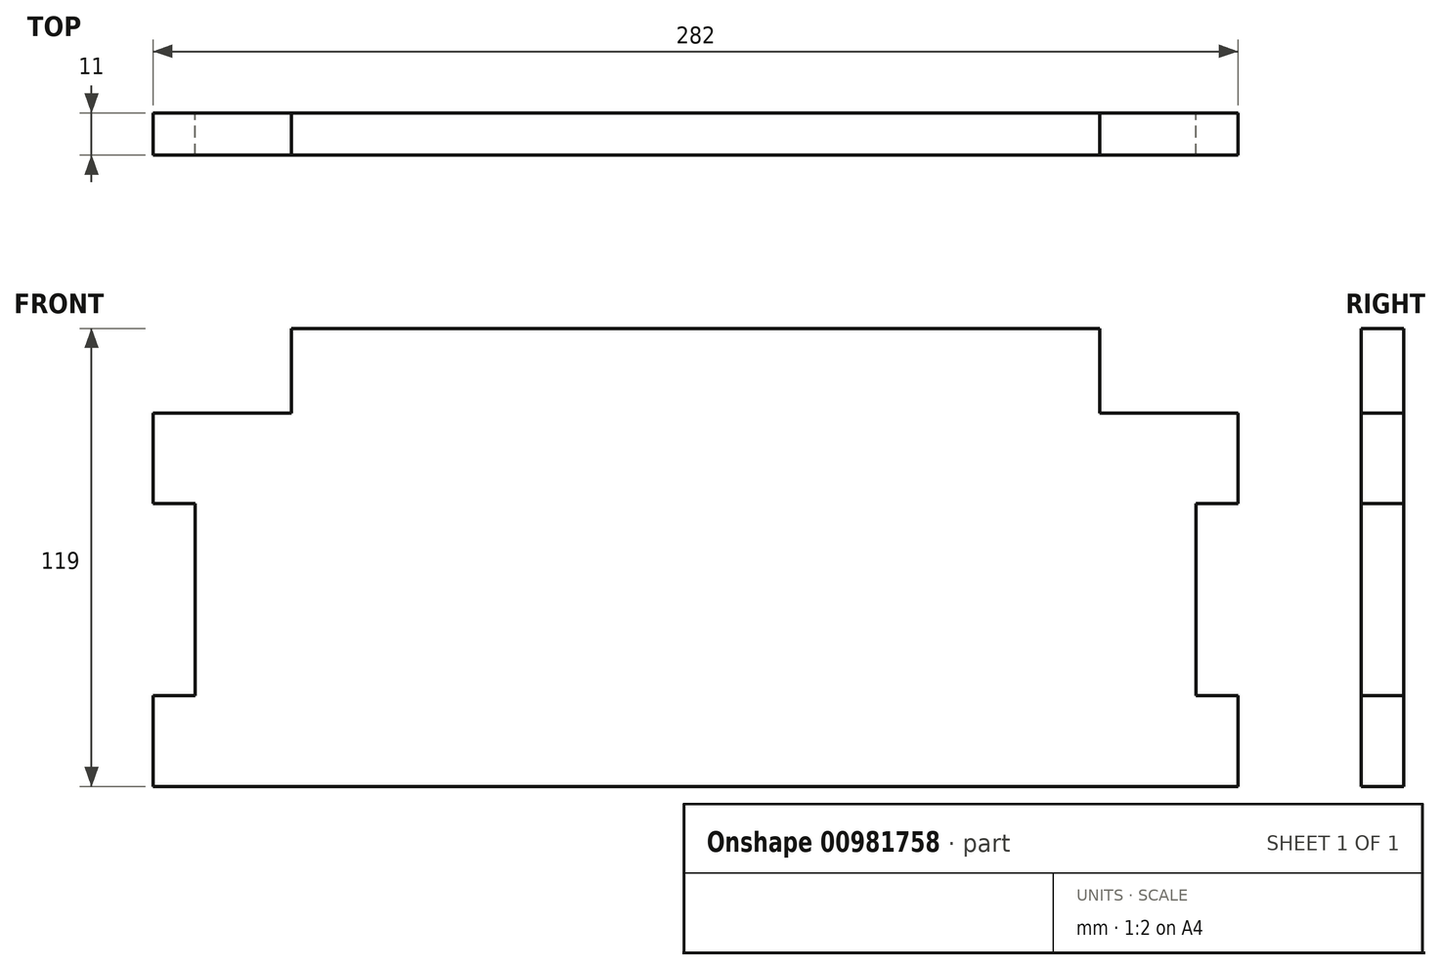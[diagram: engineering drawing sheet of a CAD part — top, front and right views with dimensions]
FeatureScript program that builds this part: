
annotation { "Feature Type Name" : "Feature", "Feature Type Description" : "" }
export const myFeature = defineFeature(function(context is Context, id is Id, definition is map)
    precondition{}
    {
        {
            var Q0;
            Q0=qCreatedBy(makeId("Front.planeOp"),FACE);
            var sketch = newSketch(context, id + "F0", { "sketchPlane" : qUnion([Q0])});
            skLineSegment(sketch, "E0", {"start": v(141, -59.5) * mm, "end": v(141, -36) * mm});
            skLineSegment(sketch, "E1", {"start": v(141, 14) * mm, "end": v(141, 37.5) * mm});
            skLineSegment(sketch, "E2", {"start": v(130, -36) * mm, "end": v(130, 14) * mm});
            skLineSegment(sketch, "E3", {"start": v(-141, -59.5) * mm, "end": v(-141, -36) * mm});
            skLineSegment(sketch, "E4", {"start": v(-141, 14) * mm, "end": v(-141, 37.5) * mm});
            skLineSegment(sketch, "E5", {"start": v(-141, -59.5) * mm, "end": v(141, -59.5) * mm});
            skLineSegment(sketch, "E6", {"start": v(-141, 37.5) * mm, "end": v(-105, 37.5) * mm});
            skLineSegment(sketch, "E7", {"start": v(105, 37.5) * mm, "end": v(141, 37.5) * mm});
            skLineSegment(sketch, "E8", {"start": v(-105, 59.5) * mm, "end": v(105, 59.5) * mm});
            skLineSegment(sketch, "E9", {"start": v(-105, 37.5) * mm, "end": v(-105, 59.5) * mm});
            skLineSegment(sketch, "E10", {"start": v(105, 37.5) * mm, "end": v(105, 59.5) * mm});
            skLineSegment(sketch, "E11", {"start": v(141, 14) * mm, "end": v(130, 14) * mm});
            skLineSegment(sketch, "E12", {"start": v(141, -36) * mm, "end": v(130, -36) * mm});
            skLineSegment(sketch, "E13", {"start": v(-130, -36) * mm, "end": v(-130, 14) * mm});
            skLineSegment(sketch, "E14", {"start": v(-141, 14) * mm, "end": v(-130, 14) * mm});
            skLineSegment(sketch, "E15", {"start": v(-141, -36) * mm, "end": v(-130, -36) * mm});
            skSolve(sketch);
        }
        {
            var Q0;
            Q0=makeQuery(id+"F0.imprint","IMPRINT",FACE,{"disambiguationData":[TD([[makeQuery(id+"F0.imprint","IMPRINT",EDGE,{"derivedFrom":sQuery(id+"F0.wireOp",EDGE,"E0")}),1.0]])]});
            extrude(context, id + "F1", {"entities" : qUnion([Q0]), "depth" : 11 * mm, "offsetDistance" : 25 * mm});
        }
    });
